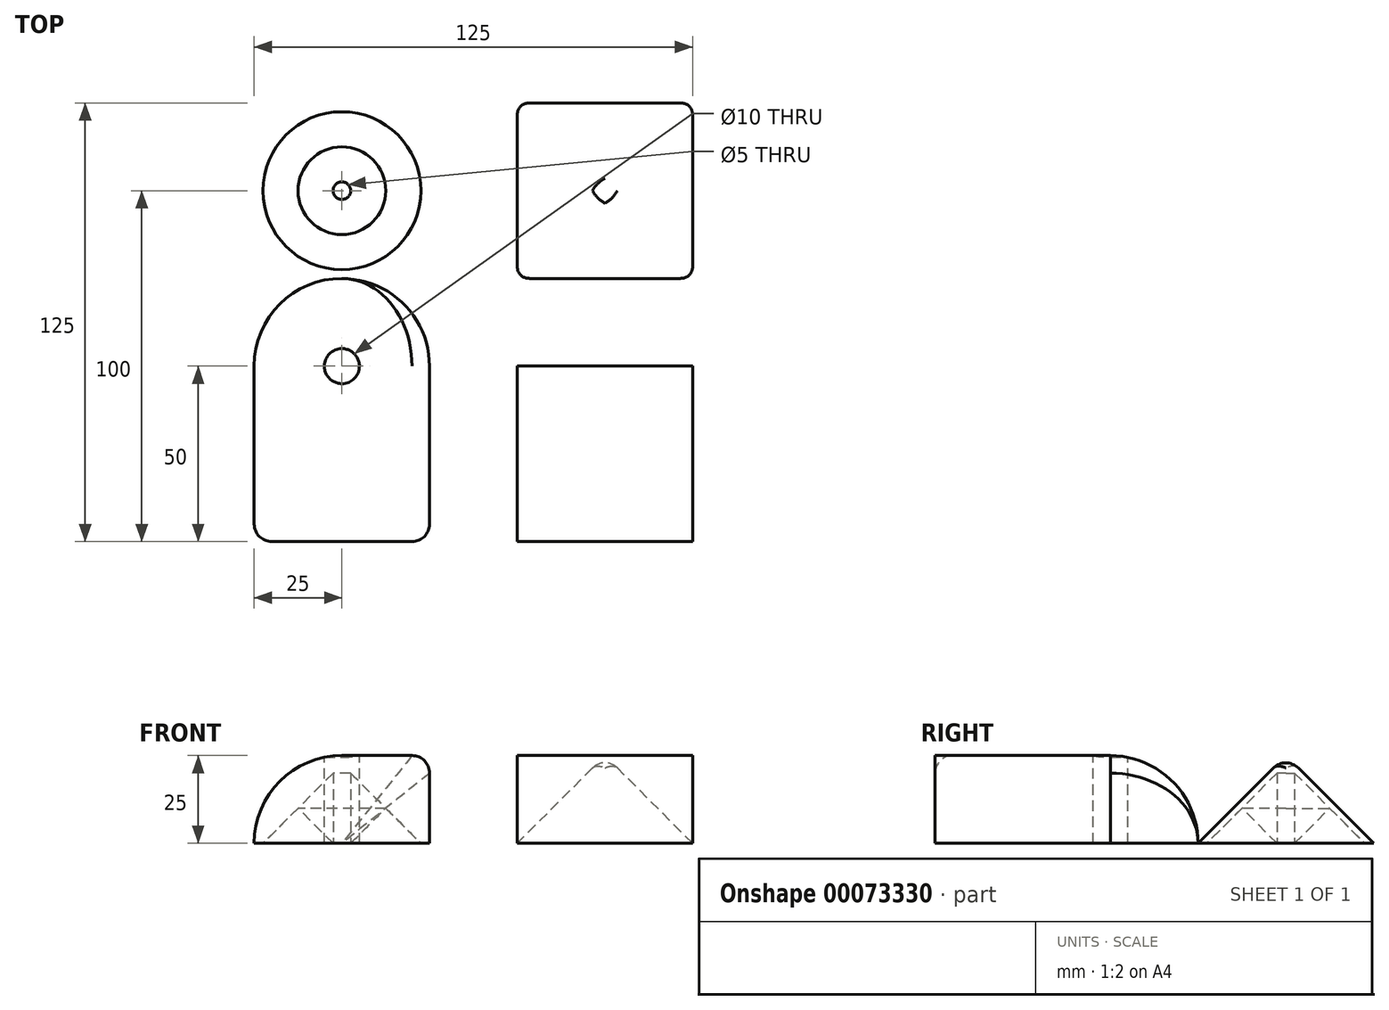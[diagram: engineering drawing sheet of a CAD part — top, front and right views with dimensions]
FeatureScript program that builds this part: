
annotation { "Feature Type Name" : "Feature", "Feature Type Description" : "" }
export const myFeature = defineFeature(function(context is Context, id is Id, definition is map)
    precondition{}
    {
        {
            var Q0;
            Q0=qCreatedBy(makeId("Top.planeOp"),FACE);
            var sketch = newSketch(context, id + "F0", { "sketchPlane" : qUnion([Q0])});
            skLineSegment(sketch, "E0.rect.bottom", {"start": v(-25, 25) * mm, "end": v(25, 25) * mm});
            skLineSegment(sketch, "E0.rect.top", {"start": v(-25, -25) * mm, "end": v(25, -25) * mm});
            skLineSegment(sketch, "E0.rect.left", {"start": v(-25, 25) * mm, "end": v(-25, -25) * mm});
            skLineSegment(sketch, "E0.rect.right", {"start": v(25, 25) * mm, "end": v(25, -25) * mm});
            skPoint(sketch, "E0.rect.middle", {"position": v(0, 0) * mm});
            skLineSegment(sketch, "E1.rect.top", {"start": v(-100, -25) * mm, "end": v(-50, -25) * mm});
            skLineSegment(sketch, "E1.rect.left", {"start": v(-100, 25) * mm, "end": v(-100, -25) * mm});
            skLineSegment(sketch, "E1.rect.right", {"start": v(-50, 25) * mm, "end": v(-50, -25) * mm});
            skPoint(sketch, "E1.rect.middle", {"position": v(-75, 0) * mm});
            skLineSegment(sketch, "E2.rect.bottom", {"start": v(25, 50) * mm, "end": v(-25, 50) * mm});
            skLineSegment(sketch, "E2.rect.top", {"start": v(25, 100) * mm, "end": v(-25, 100) * mm});
            skLineSegment(sketch, "E2.rect.left", {"start": v(25, 50) * mm, "end": v(25, 100) * mm});
            skLineSegment(sketch, "E2.rect.right", {"start": v(-25, 50) * mm, "end": v(-25, 100) * mm});
            skPoint(sketch, "E2.rect.middle", {"position": v(0, 75) * mm});
            skArc(sketch, "E3", {"start": v(-50, 25) * mm, "mid": v(-75, 50) * mm, "end": v(-100, 25) * mm});
            skLineSegment(sketch, "E4", {"start": v(-75, 50) * mm, "end": v(-75, -25) * mm});
            skCircle(sketch, "E5", {"center": v(-75, 75) * mm, "radius": 22.5 * mm});
            skCircle(sketch, "E6", {"center": v(-75, 75) * mm, "radius": 2.5 * mm});
            skSolve(sketch);
        }
        {
            var Q0;
            Q0=makeQuery(id+"F0.imprint","IMPRINT",FACE,{"disambiguationData":[TD([[makeQuery(id+"F0.imprint","IMPRINT",EDGE,{"derivedFrom":sQuery(id+"F0.wireOp",EDGE,"E0.rect.bottom")}),-1.0]])]});
            var Q1;
            {var subQ0=sQuery(id+"F0.wireOp",EDGE,"E1.rect.right");Q1=makeQuery(id+"F0.imprint","IMPRINT",FACE,{"disambiguationData":[TD([[makeQuery(id+"F0.imprint","IMPRINT",EDGE,{"derivedFrom":subQ0}),-1.0]])]});}
            extrude(context, id + "F1", {"entities" : qUnion([Q0, Q1]), "depth" : 25 * mm});
        }
        {
            var Q0;
            {var subQ0=sQuery(id+"F0.wireOp",EDGE,"E1.rect.left");Q0=makeQuery(id+"F0.imprint","IMPRINT",FACE,{"disambiguationData":[TD([[makeQuery(id+"F0.imprint","IMPRINT",EDGE,{"derivedFrom":subQ0}),1.0]])]});}
            var Q1;
            Q1=sQuery(id+"F0.wireOp",EDGE,"E4");
            revolve(context, id + "F2", {"operationType" : NewBodyOperationType.ADD, "entities" : qUnion([Q0]), "axis" : qUnion([Q1]), "revolveType" : RevolveType.ONE_DIRECTION, "oppositeDirection" : true, "angle" : 90 * degree});
        }
        {
            var Q0;
            Q0=makeQuery(id+"F1.opExtrude","SWEPT_FACE",FACE,{"disambiguationData":[OSD([sQuery(id+"F0.wireOp",EDGE,"E4")])]});
            extrude(context, id + "F3", {"entities" : qUnion([Q0]), "operationType" : NewBodyOperationType.REMOVE, "oppositeDirection" : true, "depth" : 25 * mm});
        }
        {
            var Q0;
            {var subQ0=sQuery(id+"F0.wireOp",EDGE,"E3");Q0=makeQuery(id+"F3.boolean.opBoolean","INTERSECT",EDGE,{"derivedFrom":[makeQuery(id+"F1.opExtrude","SWEPT_FACE",FACE,{"disambiguationData":[OSD([subQ0])]}),makeQuery(id+"F3.opExtrude","SWEPT_FACE",FACE,{"disambiguationData":[OSD([subQ0])]})]});}
            var Q1;
            Q1=makeQuery(id+"F1.opExtrude","SWEPT_EDGE",EDGE,{"disambiguationData":[OSD([sQuery(id+"F0.wireOp",EDGE,"E1.rect.top"),sQuery(id+"F0.wireOp",EDGE,"E1.rect.right")])]});
            var Q2;
            Q2=makeQuery(id+"F1.opExtrude","CAP_EDGE",EDGE,{"disambiguationData":[OSD([sQuery(id+"F0.wireOp",EDGE,"E1.rect.top")])],"isStart":false});
            fillet(context, id + "F4", {"entities" : qUnion([Q0, Q1, Q2]), "radius" : 5 * mm, "tangentPropagation" : true, "allowEdgeOverflow" : false});
        }
        {
            var Q0;
            Q0=makeQuery(id+"F0.imprint","IMPRINT",FACE,{"disambiguationData":[TD([[makeQuery(id+"F0.imprint","IMPRINT",EDGE,{"derivedFrom":sQuery(id+"F0.wireOp",EDGE,"E2.rect.bottom")}),-1.0]])]});
            var Q1;
            Q1=makeQuery(id+"F0.imprint","IMPRINT",FACE,{"disambiguationData":[TD([[makeQuery(id+"F0.imprint","IMPRINT",EDGE,{"derivedFrom":sQuery(id+"F0.wireOp",EDGE,"E5")}),1.0]])]});
            var Q2;
            Q2=makeQuery(id+"F0.imprint","IMPRINT",FACE,{"disambiguationData":[TD([[makeQuery(id+"F0.imprint","IMPRINT",EDGE,{"derivedFrom":sQuery(id+"F0.wireOp",EDGE,"E6")}),1.0]])]});
            extrude(context, id + "F5", {"entities" : qUnion([Q0, Q1, Q2]), "depth" : 50 * mm, "hasDraft" : true, "draftAngle" : 45 * degree, "draftPullDirection" : true});
        }
        {
            var Q0;
            Q0=makeQuery(id+"F5.opExtrude","SWEPT_EDGE",EDGE,{"disambiguationData":[OSD([sQuery(id+"F0.wireOp",EDGE,"E2.rect.top"),sQuery(id+"F0.wireOp",EDGE,"E2.rect.left")])]});
            var Q1;
            Q1=makeQuery(id+"F5.opExtrude","SWEPT_EDGE",EDGE,{"disambiguationData":[OSD([sQuery(id+"F0.wireOp",EDGE,"E2.rect.top"),sQuery(id+"F0.wireOp",EDGE,"E2.rect.right")])]});
            var Q2;
            Q2=makeQuery(id+"F5.opExtrude","SWEPT_EDGE",EDGE,{"disambiguationData":[OSD([sQuery(id+"F0.wireOp",EDGE,"E2.rect.bottom"),sQuery(id+"F0.wireOp",EDGE,"E2.rect.right")])]});
            var Q3;
            Q3=makeQuery(id+"F5.opExtrude","SWEPT_EDGE",EDGE,{"disambiguationData":[OSD([sQuery(id+"F0.wireOp",EDGE,"E2.rect.bottom"),sQuery(id+"F0.wireOp",EDGE,"E2.rect.left")])]});
            fillet(context, id + "F6", {"entities" : qUnion([Q0, Q1, Q2, Q3]), "radius" : 5 * mm, "tangentPropagation" : true, "allowEdgeOverflow" : false});
        }
        {
            var Q0;
            Q0=makeQuery(id+"F0.imprint","IMPRINT",FACE,{"disambiguationData":[TD([[makeQuery(id+"F0.imprint","IMPRINT",EDGE,{"derivedFrom":sQuery(id+"F0.wireOp",EDGE,"E5")}),1.0]])]});
            extrude(context, id + "F7", {"entities" : qUnion([Q0]), "depth" : 25 * mm, "hasDraft" : true, "draftAngle" : 45 * degree, "draftPullDirection" : true});
        }
        {
            var Q0;
            Q0=makeQuery(id+"F1.opExtrude","CAP_FACE",FACE,{"disambiguationData":[OSD([sQuery(id+"F0.wireOp",EDGE,"E1.rect.top"),sQuery(id+"F0.wireOp",EDGE,"E1.rect.right"),sQuery(id+"F0.wireOp",EDGE,"E3"),sQuery(id+"F0.wireOp",EDGE,"E4")])],"isStart":false});
            var sketch = newSketch(context, id + "F8", { "sketchPlane" : qUnion([Q0])});
            skCircle(sketch, "E7", {"center": v(-75, 25) * mm, "radius": 5 * mm});
            skSolve(sketch);
        }
        {
            var Q0;
            {var subQ0=sQuery(id+"F8.wireOp",EDGE,"E7");var subQ1=sQuery(id+"F0.wireOp",EDGE,"E1.rect.left");var subQ2=makeQuery(id+"F3.boolean.opBoolean","COPY",EDGE,{"derivedFrom":makeQuery(id+"F3.opExtrude","SWEPT_EDGE",EDGE,{"disambiguationData":[OSD([subQ1,sQuery(id+"F0.wireOp",EDGE,"E3")])]})});var subQ3=makeQuery(id+"F8.imprint","INTERSECT",VERTEX,{"derivedFrom":[subQ2,subQ0]});Q0=makeQuery(id+"F8.imprint","IMPRINT",FACE,{"disambiguationData":[TD([[makeQuery(id+"F8.imprint","IMPRINT",EDGE,{"disambiguationData":[TD([[subQ3,1.0]])],"derivedFrom":subQ0}),1.0]])]});}
            var Q1;
            {var subQ0=sQuery(id+"F8.wireOp",EDGE,"E7");var subQ1=sQuery(id+"F0.wireOp",EDGE,"E1.rect.left");var subQ2=makeQuery(id+"F3.boolean.opBoolean","COPY",EDGE,{"derivedFrom":makeQuery(id+"F3.opExtrude","SWEPT_EDGE",EDGE,{"disambiguationData":[OSD([subQ1,sQuery(id+"F0.wireOp",EDGE,"E3")])]})});var subQ3=makeQuery(id+"F8.imprint","INTERSECT",VERTEX,{"derivedFrom":[subQ2,subQ0]});Q1=makeQuery(id+"F8.imprint","IMPRINT",FACE,{"disambiguationData":[TD([[makeQuery(id+"F8.imprint","IMPRINT",EDGE,{"disambiguationData":[TD([[subQ3,-1.0]])],"derivedFrom":subQ0}),1.0]])]});}
            extrude(context, id + "F9", {"entities" : qUnion([Q0, Q1]), "operationType" : NewBodyOperationType.REMOVE, "oppositeDirection" : true, "depth" : 25 * mm});
        }
        {
            var Q0;
            Q0=makeQuery(id+"F0.imprint","IMPRINT",FACE,{"disambiguationData":[TD([[makeQuery(id+"F0.imprint","IMPRINT",EDGE,{"derivedFrom":sQuery(id+"F0.wireOp",EDGE,"E6")}),1.0]])]});
            extrude(context, id + "F10", {"entities" : qUnion([Q0]), "operationType" : NewBodyOperationType.REMOVE, "depth" : 26.27 * mm});
        }
    });
